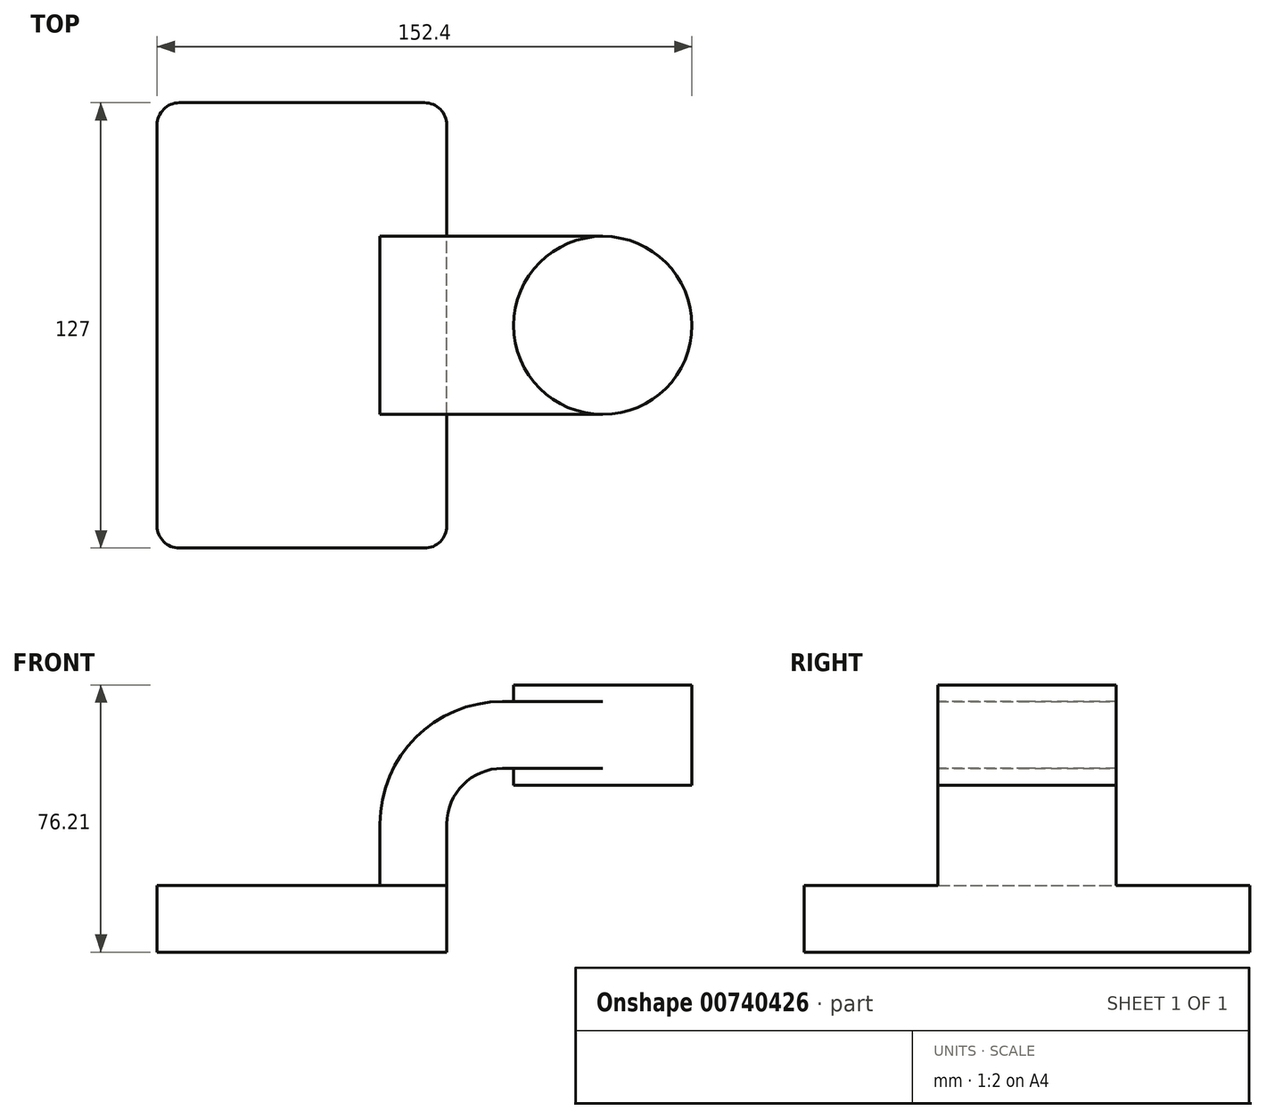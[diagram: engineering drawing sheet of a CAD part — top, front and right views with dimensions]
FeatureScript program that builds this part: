
annotation { "Feature Type Name" : "Feature", "Feature Type Description" : "" }
export const myFeature = defineFeature(function(context is Context, id is Id, definition is map)
    precondition{}
    {
        {
            var Q0;
            Q0=qCreatedBy(makeId("Front.planeOp"),FACE);
            var sketch = newSketch(context, id + "F0", { "sketchPlane" : qUnion([Q0])});
            skLineSegment(sketch, "E0.bottom", {"start": v(41.28, -9.52) * mm, "end": v(-41.28, -9.53) * mm});
            skLineSegment(sketch, "E0.top", {"start": v(41.27, 9.53) * mm, "end": v(-41.28, 9.53) * mm});
            skLineSegment(sketch, "E0.left", {"start": v(41.28, -9.52) * mm, "end": v(41.28, 9.53) * mm});
            skLineSegment(sketch, "E0.right", {"start": v(-41.28, -9.53) * mm, "end": v(-41.28, 9.53) * mm});
            skPoint(sketch, "E0.middle", {"position": v(0, 0) * mm});
            skLineSegment(sketch, "E1.bottom", {"start": v(60.33, 38.1) * mm, "end": v(111.13, 38.1) * mm});
            skLineSegment(sketch, "E1.top", {"start": v(60.32, 66.68) * mm, "end": v(111.13, 66.68) * mm});
            skLineSegment(sketch, "E1.left", {"start": v(60.33, 38.1) * mm, "end": v(60.32, 66.68) * mm});
            skLineSegment(sketch, "E1.right", {"start": v(111.13, 38.1) * mm, "end": v(111.12, 66.68) * mm});
            skPoint(sketch, "E1.middle", {"position": v(85.72, 52.39) * mm});
            skLineSegment(sketch, "E2", {"start": v(41.27, 9.53) * mm, "end": v(41.27, 27) * mm});
            skArc(sketch, "E3", {"start": v(41.27, 27) * mm, "mid": v(45.92, 38.23) * mm, "end": v(57.15, 42.88) * mm});
            skLineSegment(sketch, "E4", {"start": v(57.15, 42.88) * mm, "end": v(85.73, 42.88) * mm});
            skPoint(sketch, "E5.endSnap0", {"position": v(85.73, 66.68) * mm});
            skLineSegment(sketch, "E6.0", {"start": v(57.15, 61.93) * mm, "end": v(85.76, 61.93) * mm});
            skArc(sketch, "E6.1", {"start": v(22.23, 27) * mm, "mid": v(32.45, 51.7) * mm, "end": v(57.15, 61.93) * mm});
            skLineSegment(sketch, "E6.2", {"start": v(22.22, 9.53) * mm, "end": v(22.22, 27) * mm});
            skLineSegment(sketch, "E7", {"start": v(85.73, 38.1) * mm, "end": v(85.73, 66.68) * mm});
            skFitSpline(sketch, "E8", {"points": [v(-41.28, 9.52) * mm, v(57.15, 61.93) * mm], "startDerivative": vector(40.9, 81.24) * mm, "endDerivative": vector(129.26, -13.52) * mm});
            skSolve(sketch);
        }
        {
            var Q0;
            Q0=makeQuery(id+"F0.imprint","IMPRINT",FACE,{"disambiguationData":[TD([[makeQuery(id+"F0.imprint","IMPRINT",EDGE,{"derivedFrom":sQuery(id+"F0.wireOp",EDGE,"E0.bottom")}),-1.0]])]});
            extrude(context, id + "F1", {"entities" : qUnion([Q0]), "endBound" : BoundingType.SYMMETRIC, "depth" : 127 * mm});
        }
        {
            var Q0;
            {var subQ1=sQuery(id+"F0.wireOp",EDGE,"E2");Q0=makeQuery(id+"F0.imprint","IMPRINT",FACE,{"disambiguationData":[TD([[makeQuery(id+"F0.imprint","IMPRINT",EDGE,{"derivedFrom":subQ1}),1.0]])]});}
            var Q1;
            {var subQ0=sQuery(id+"F0.wireOp",EDGE,"E4");var subQ1=sQuery(id+"F0.wireOp",EDGE,"E1.left");var subQ2=makeQuery(id+"F0.imprint","INTERSECT",VERTEX,{"derivedFrom":[subQ1,subQ0]});Q1=makeQuery(id+"F0.imprint","IMPRINT",FACE,{"disambiguationData":[TD([[makeQuery(id+"F0.imprint","IMPRINT",EDGE,{"disambiguationData":[TD([[subQ2,-1.0]])],"derivedFrom":subQ1}),-1.0]])]});}
            extrude(context, id + "F2", {"entities" : qUnion([Q0, Q1]), "operationType" : NewBodyOperationType.ADD, "endBound" : BoundingType.SYMMETRIC, "depth" : 50.8 * mm});
        }
        {
            var Q0;
            {var subQ0=sQuery(id+"F0.wireOp",EDGE,"E1.right");Q0=makeQuery(id+"F0.imprint","IMPRINT",FACE,{"disambiguationData":[TD([[makeQuery(id+"F0.imprint","IMPRINT",EDGE,{"derivedFrom":subQ0}),1.0]])]});}
            var Q1;
            Q1=sQuery(id+"F0.wireOp",EDGE,"E7");
            revolve(context, id + "F3", {"operationType" : NewBodyOperationType.ADD, "entities" : qUnion([Q0]), "axis" : qUnion([Q1]), "revolveType" : RevolveType.FULL});
        }
        {
            var Q0;
            Q0=makeQuery(id+"F0.imprint","IMPRINT",FACE,{"disambiguationData":[TD([[makeQuery(id+"F0.imprint","IMPRINT",EDGE,{"derivedFrom":sQuery(id+"F0.wireOp",EDGE,"E6.1")}),1.0]])]});
            extrude(context, id + "F4", {"entities" : qUnion([Q0]), "operationType" : NewBodyOperationType.ADD, "endBound" : BoundingType.SYMMETRIC, "depth" : 15.88 * mm});
        }
        {
            var Q0;
            Q0=makeQuery(id+"F1.opExtrude","CAP_EDGE",EDGE,{"disambiguationData":[OSD([sQuery(id+"F0.wireOp",EDGE,"E0.right")])],"isStart":true});
            var Q1;
            Q1=makeQuery(id+"F1.opExtrude","CAP_EDGE",EDGE,{"disambiguationData":[OSD([sQuery(id+"F0.wireOp",EDGE,"E0.right")])],"isStart":false});
            var Q2;
            Q2=makeQuery(id+"F1.opExtrude","CAP_EDGE",EDGE,{"disambiguationData":[OSD([sQuery(id+"F0.wireOp",EDGE,"E0.left")])],"isStart":false});
            var Q3;
            Q3=makeQuery(id+"F1.opExtrude","CAP_EDGE",EDGE,{"disambiguationData":[OSD([sQuery(id+"F0.wireOp",EDGE,"E0.left")])],"isStart":true});
            fillet(context, id + "F5", {"entities" : qUnion([Q0, Q1, Q2, Q3]), "radius" : 6.35 * mm, "tangentPropagation" : true, "allowEdgeOverflow" : false});
        }
    });
